# Revit family: Profilhalter, VA
name_source: partatom
category: HLS-Bauteile
revit_build: Autodesk Revit 2017 (Build: 20190507_1515(x64)
units: mm (PartAtom-declared; Revit-internal decimal feet)

## family parameters
Arbeitsebenenbasiert = Ja
Beim Laden mit Abzugskörper schneiden = Nein
Bemaßung runder Anschluss = Durchmesser verwenden
Gemeinsam genutzt = Ja
Immer vertikal = Nein
Raumberechnungspunkt = Nein
Teiletyp = Normal

## types (4) — shared parameters
Anzugsmoment = 0.00 kN-m
Fabrikat = MEFA
Firma = MEFA Befestigungs- und Montagesysteme GmbH
Material = Edelstahl
Vorgabe-Ansicht = 1219 mm
max. zul. Last = 0.00 kN
vpe = 1 St

## per-type parameters (varying)
| type | Artikelnummer | B | Breite | D | Gewicht | Gewicht pro Bauteil | H | Höhe | Kurztext1 | Kurztext2 | L | Lochdurchmesser | Länge | Materialname | Profiltyp | Stärke Material | für Gewinde |
| Profilhalter 27, V2A | 0809513 | 20 mm  [stored 0.0656168 ft] | 20 mm  [stored 0.0656168 ft] | 11 mm | 0.01 kg | 0.01 kg | 8 mm  [stored 0.0262467 ft] | 8 mm | Profilhalter C-Profil 27 V2A | Bohrung 10.5 mm für Gewinde M10 | 28 mm  [stored 0.0918635 ft] | 10.5 mm | 28 mm  [stored 0.0918635 ft] | V2A | 27 | 2 mm  [stored 0.00656168 ft] | M10 |
| Profilhalter 35, V2A | 0809511 | 30 mm  [stored 0.0984252 ft] | 30 mm  [stored 0.0984252 ft] | 13 mm | 0.04 kg | 0.04 kg | 12 mm  [stored 0.0393701 ft] | 12 mm | Profilhalter C-Profil 35 V2A | Bohrung 13 mm für Gewinde M12 | 36 mm  [stored 0.11811 ft] | 13 mm | 36 mm  [stored 0.11811 ft] | V2A | 35 | 3 mm  [stored 0.00984252 ft] | M12 |
| Profilhalter 45, V2A | 0480629 | 35 mm  [stored 0.114829 ft] | 35 mm  [stored 0.114829 ft] | 13 mm | 0.09 kg | 0.09 kg | 15 mm  [stored 0.0492126 ft] | 15 mm | Profilhalter C-Profil 45 V2A | Bohrung 13 mm für Gewinde M12 | 46 mm  [stored 0.150919 ft] | 13 mm | 46 mm  [stored 0.150919 ft] | V2A | 45 | 4 mm  [stored 0.0131234 ft] | M12 |
| Profilhalter 45, V4A | 0481629 | 35 mm  [stored 0.114829 ft] | 35 mm  [stored 0.114829 ft] | 13 mm | 0.09 kg | 0.09 kg | 15 mm  [stored 0.0492126 ft] | 15 mm | Profilhalter C-Profil 45 V4A | Bohrung 13 mm für Gewinde M12 | 46 mm  [stored 0.150919 ft] | 13 mm | 46 mm  [stored 0.150919 ft] | V4A | 45 | 4 mm  [stored 0.0131234 ft] | M12 |

note: [stored X ft] marks values corroborated as IEEE doubles in the binary element streams (Revit-internal decimal feet)
